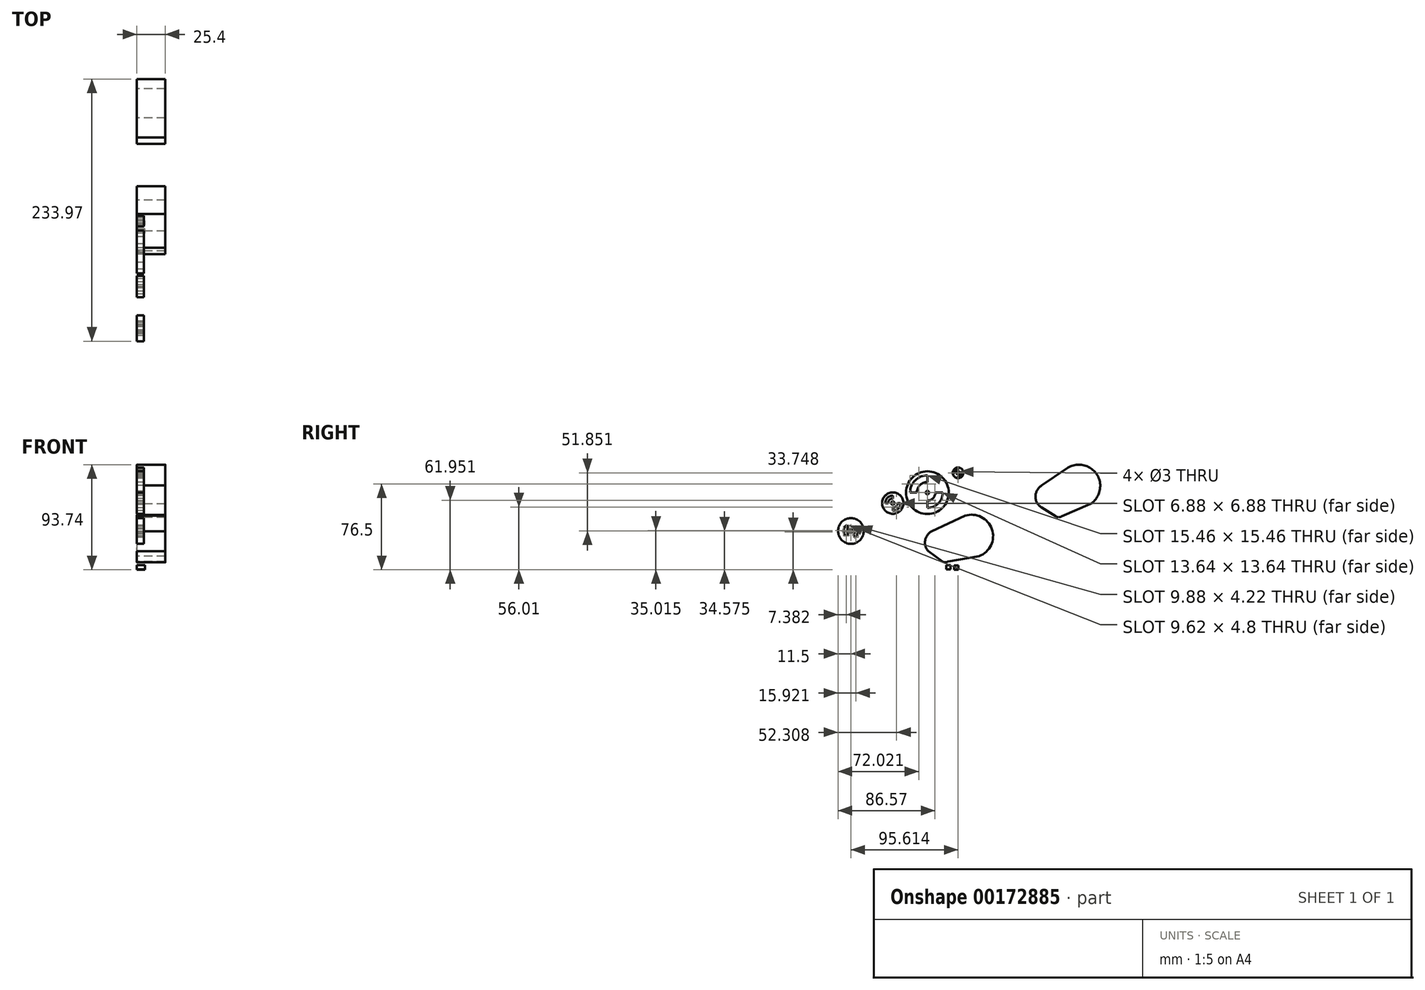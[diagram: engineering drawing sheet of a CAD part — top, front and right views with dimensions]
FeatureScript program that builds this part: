
annotation { "Feature Type Name" : "Feature", "Feature Type Description" : "" }
export const myFeature = defineFeature(function(context is Context, id is Id, definition is map)
    precondition{}
    {
        {
            var Q0;
            Q0=qCreatedBy(makeId("Right.planeOp"),FACE);
            var sketch = newSketch(context, id + "F0", { "sketchPlane" : qUnion([Q0])});
            skCircle(sketch, "E0", {"center": v(-94.35, 39) * mm, "radius": 9.53 * mm});
            skCircle(sketch, "E1", {"center": v(-63.47, 48.33) * mm, "radius": 19.05 * mm});
            skCircle(sketch, "E2", {"center": v(-36.1, 65.99) * mm, "radius": 4.76 * mm});
            skPoint(sketch, "E3.orphan", {"position": v(0, 71.85) * mm});
            skCircle(sketch, "E4", {"center": v(-63.47, 48.33) * mm, "radius": 1.5 * mm});
            skCircle(sketch, "E5", {"center": v(-36.1, 65.99) * mm, "radius": 1.5 * mm});
            skCircle(sketch, "E6", {"center": v(-94.35, 39) * mm, "radius": 1.5 * mm});
            skArc(sketch, "E7", {"start": v(-63.47, 41.26) * mm, "mid": v(-58.47, 43.33) * mm, "end": v(-56.4, 48.33) * mm});
            skArc(sketch, "E8", {"start": v(-63.47, 34.69) * mm, "mid": v(-53.82, 38.69) * mm, "end": v(-49.83, 48.33) * mm});
            skLineSegment(sketch, "E9", {"start": v(-56.4, 48.33) * mm, "end": v(-49.83, 48.33) * mm});
            skLineSegment(sketch, "E10", {"start": v(-63.47, 41.26) * mm, "end": v(-63.47, 34.69) * mm});
            skArc(sketch, "E11", {"start": v(-72.88, 48.33) * mm, "mid": v(-70.13, 54.99) * mm, "end": v(-63.47, 57.74) * mm});
            skArc(sketch, "E12", {"start": v(-78.93, 48.33) * mm, "mid": v(-74.4, 59.26) * mm, "end": v(-63.47, 63.79) * mm});
            skLineSegment(sketch, "E13", {"start": v(-63.47, 63.79) * mm, "end": v(-63.47, 57.74) * mm});
            skLineSegment(sketch, "E14", {"start": v(-72.88, 48.33) * mm, "end": v(-78.93, 48.33) * mm});
            skArc(sketch, "E15", {"start": v(-94.35, 32.13) * mm, "mid": v(-89.49, 34.15) * mm, "end": v(-87.47, 39) * mm});
            skArc(sketch, "E16", {"start": v(-94.35, 34.89) * mm, "mid": v(-91.44, 36.1) * mm, "end": v(-90.23, 39) * mm});
            skArc(sketch, "E17", {"start": v(-101.06, 39) * mm, "mid": v(-99.1, 43.76) * mm, "end": v(-94.35, 45.72) * mm});
            skArc(sketch, "E18", {"start": v(-98.5, 39) * mm, "mid": v(-97.29, 41.95) * mm, "end": v(-94.35, 43.16) * mm});
            skLineSegment(sketch, "E19", {"start": v(-94.35, 45.72) * mm, "end": v(-94.35, 43.16) * mm});
            skLineSegment(sketch, "E20", {"start": v(-101.06, 39) * mm, "end": v(-98.5, 39) * mm});
            skLineSegment(sketch, "E21", {"start": v(-90.23, 39) * mm, "end": v(-87.47, 39) * mm});
            skLineSegment(sketch, "E22", {"start": v(-94.35, 34.89) * mm, "end": v(-94.35, 32.13) * mm});
            skArc(sketch, "E23", {"start": v(-36.1, 63.1) * mm, "mid": v(-34.06, 63.94) * mm, "end": v(-33.21, 65.99) * mm});
            skArc(sketch, "E24", {"start": v(-38.96, 65.99) * mm, "mid": v(-38.13, 68) * mm, "end": v(-36.1, 68.85) * mm});
            skArc(sketch, "E25", {"start": v(-36.1, 61.66) * mm, "mid": v(-33.05, 62.93) * mm, "end": v(-31.78, 65.99) * mm});
            skArc(sketch, "E26", {"start": v(-40.4, 65.99) * mm, "mid": v(-39.14, 69.02) * mm, "end": v(-36.1, 70.27) * mm});
            skLineSegment(sketch, "E27", {"start": v(-36.1, 70.27) * mm, "end": v(-36.1, 68.85) * mm});
            skLineSegment(sketch, "E28", {"start": v(-40.4, 65.99) * mm, "end": v(-38.96, 65.99) * mm});
            skLineSegment(sketch, "E29", {"start": v(-36.1, 63.1) * mm, "end": v(-36.1, 61.66) * mm});
            skLineSegment(sketch, "E30", {"start": v(-33.21, 65.99) * mm, "end": v(-31.78, 65.99) * mm});
            skCircle(sketch, "E31", {"center": v(-131.72, 14.14) * mm, "radius": 11.5 * mm});
            skCircle(sketch, "E32", {"center": v(-131.72, 14.14) * mm, "radius": 1.5 * mm});
            skArc(sketch, "E33", {"start": v(-128.66, 8.37) * mm, "mid": v(-125.32, 12.83) * mm, "end": v(-126.65, 18.25) * mm});
            skArc(sketch, "E34", {"start": v(-136.6, 9.77) * mm, "mid": v(-138.24, 14.79) * mm, "end": v(-135.64, 19.38) * mm});
            skArc(sketch, "E35", {"start": v(-129.13, 16.54) * mm, "mid": v(-128.19, 13.94) * mm, "end": v(-129.4, 11.46) * mm});
            skArc(sketch, "E36", {"start": v(-133.8, 16.54) * mm, "mid": v(-134.9, 13.9) * mm, "end": v(-133.44, 11.46) * mm});
            skLineSegment(sketch, "E37", {"start": v(-135.64, 19.38) * mm, "end": v(-133.8, 16.54) * mm});
            skLineSegment(sketch, "E38", {"start": v(-136.6, 9.77) * mm, "end": v(-133.44, 11.46) * mm});
            skLineSegment(sketch, "E39", {"start": v(-129.13, 16.54) * mm, "end": v(-126.65, 18.25) * mm});
            skLineSegment(sketch, "E40", {"start": v(-129.4, 11.46) * mm, "end": v(-128.66, 8.37) * mm});
            skArc(sketch, "E41", {"start": v(-24.01, -9.5) * mm, "mid": v(-5.56, 14.7) * mm, "end": v(-33.93, 25.75) * mm});
            skArc(sketch, "E42", {"start": v(-58.16, 14.5) * mm, "mid": v(-65.64, 4.1) * mm, "end": v(-58.88, -6.77) * mm});
            skArc(sketch, "E43", {"start": v(-50.32, -12.97) * mm, "mid": v(-47.68, -13.88) * mm, "end": v(-44.98, -13.14) * mm});
            skLineSegment(sketch, "E44", {"start": v(-59.78, 13.75) * mm, "end": v(-29.8, 27.66) * mm});
            skLineSegment(sketch, "E45", {"start": v(-62.64, -4.04) * mm, "end": v(-50.32, -12.97) * mm});
            skLineSegment(sketch, "E46", {"start": v(-44.98, -13.14) * mm, "end": v(-17.37, -8.34) * mm});
            skArc(sketch, "E47", {"start": v(51.18, 27.09) * mm, "mid": v(53.7, 26.36) * mm, "end": v(56.22, 27.09) * mm});
            skArc(sketch, "E48", {"start": v(38.48, 54.67) * mm, "mid": v(32.96, 44.88) * mm, "end": v(38.41, 35.06) * mm});
            skLineSegment(sketch, "E49", {"start": v(38.48, 54.67) * mm, "end": v(61, 70.01) * mm});
            skLineSegment(sketch, "E50", {"start": v(38.41, 35.06) * mm, "end": v(51.18, 27.09) * mm});
            skLineSegment(sketch, "E51", {"start": v(56.22, 27.09) * mm, "end": v(82.18, 38.31) * mm});
            skArc(sketch, "E52.trimOffspring", {"start": v(76.26, 35.75) * mm, "mid": v(89.1, 62) * mm, "end": v(61, 70.01) * mm});
            skSolve(sketch);
        }
        {
            var Q0;
            Q0=qCreatedBy(makeId("Right.planeOp"),FACE);
            var sketch = newSketch(context, id + "F1", { "sketchPlane" : qUnion([Q0])});
            skLineSegment(sketch, "E53.bottom", {"start": v(-46.67, -16.4) * mm, "end": v(-42.86, -16.4) * mm});
            skLineSegment(sketch, "E53.top", {"start": v(-46.67, -20.2) * mm, "end": v(-42.86, -20.2) * mm});
            skLineSegment(sketch, "E53.left", {"start": v(-46.67, -16.4) * mm, "end": v(-46.67, -20.2) * mm});
            skLineSegment(sketch, "E53.right", {"start": v(-42.86, -16.4) * mm, "end": v(-42.86, -20.2) * mm});
            skLineSegment(sketch, "E54.bottom", {"start": v(-39.57, -16.63) * mm, "end": v(-35.76, -16.63) * mm});
            skLineSegment(sketch, "E54.top", {"start": v(-39.57, -20.44) * mm, "end": v(-35.76, -20.44) * mm});
            skLineSegment(sketch, "E54.left", {"start": v(-39.57, -16.63) * mm, "end": v(-39.57, -20.44) * mm});
            skLineSegment(sketch, "E54.right", {"start": v(-35.76, -16.63) * mm, "end": v(-35.76, -20.44) * mm});
            skSolve(sketch);
        }
        {
            var Q0;
            Q0=qSketchRegion(id+"F1",true);
            extrude(context, id + "F2", {"entities" : qUnion([Q0]), "depth" : 7.35 * mm});
        }
        {
            var Q0;
            Q0=makeQuery(id+"F0.imprint","IMPRINT",FACE,{"disambiguationData":[TD([[makeQuery(id+"F0.imprint","IMPRINT",EDGE,{"derivedFrom":sQuery(id+"F0.wireOp",EDGE,"E1")}),1.0]])]});
            var Q1;
            Q1=makeQuery(id+"F0.imprint","IMPRINT",FACE,{"disambiguationData":[TD([[makeQuery(id+"F0.imprint","IMPRINT",EDGE,{"derivedFrom":sQuery(id+"F0.wireOp",EDGE,"E2")}),1.0]])]});
            var Q2;
            Q2=makeQuery(id+"F0.imprint","IMPRINT",FACE,{"disambiguationData":[TD([[makeQuery(id+"F0.imprint","IMPRINT",EDGE,{"derivedFrom":sQuery(id+"F0.wireOp",EDGE,"E0")}),1.0]])]});
            var Q3;
            Q3=makeQuery(id+"F0.imprint","IMPRINT",FACE,{"disambiguationData":[TD([[makeQuery(id+"F0.imprint","IMPRINT",EDGE,{"derivedFrom":sQuery(id+"F0.wireOp",EDGE,"E31")}),1.0]])]});
            extrude(context, id + "F3", {"entities" : qUnion([Q0, Q1, Q2, Q3]), "depth" : 6.35 * mm});
        }
        {
            var Q0;
            {var subQ4=sQuery(id+"F0.wireOp",EDGE,"E43");Q0=makeQuery(id+"F0.imprint","IMPRINT",FACE,{"disambiguationData":[TD([[makeQuery(id+"F0.imprint","IMPRINT",EDGE,{"derivedFrom":subQ4}),1.0]])]});}
            extrude(context, id + "F4", {"entities" : qUnion([Q0]), "depth" : 25.4 * mm});
        }
        {
            var Q0;
            {var subQ1=sQuery(id+"F0.wireOp",EDGE,"E47");Q0=makeQuery(id+"F0.imprint","IMPRINT",FACE,{"disambiguationData":[TD([[makeQuery(id+"F0.imprint","IMPRINT",EDGE,{"derivedFrom":subQ1}),1.0]])]});}
            extrude(context, id + "F5", {"entities" : qUnion([Q0]), "depth" : 25.4 * mm});
        }
    });
